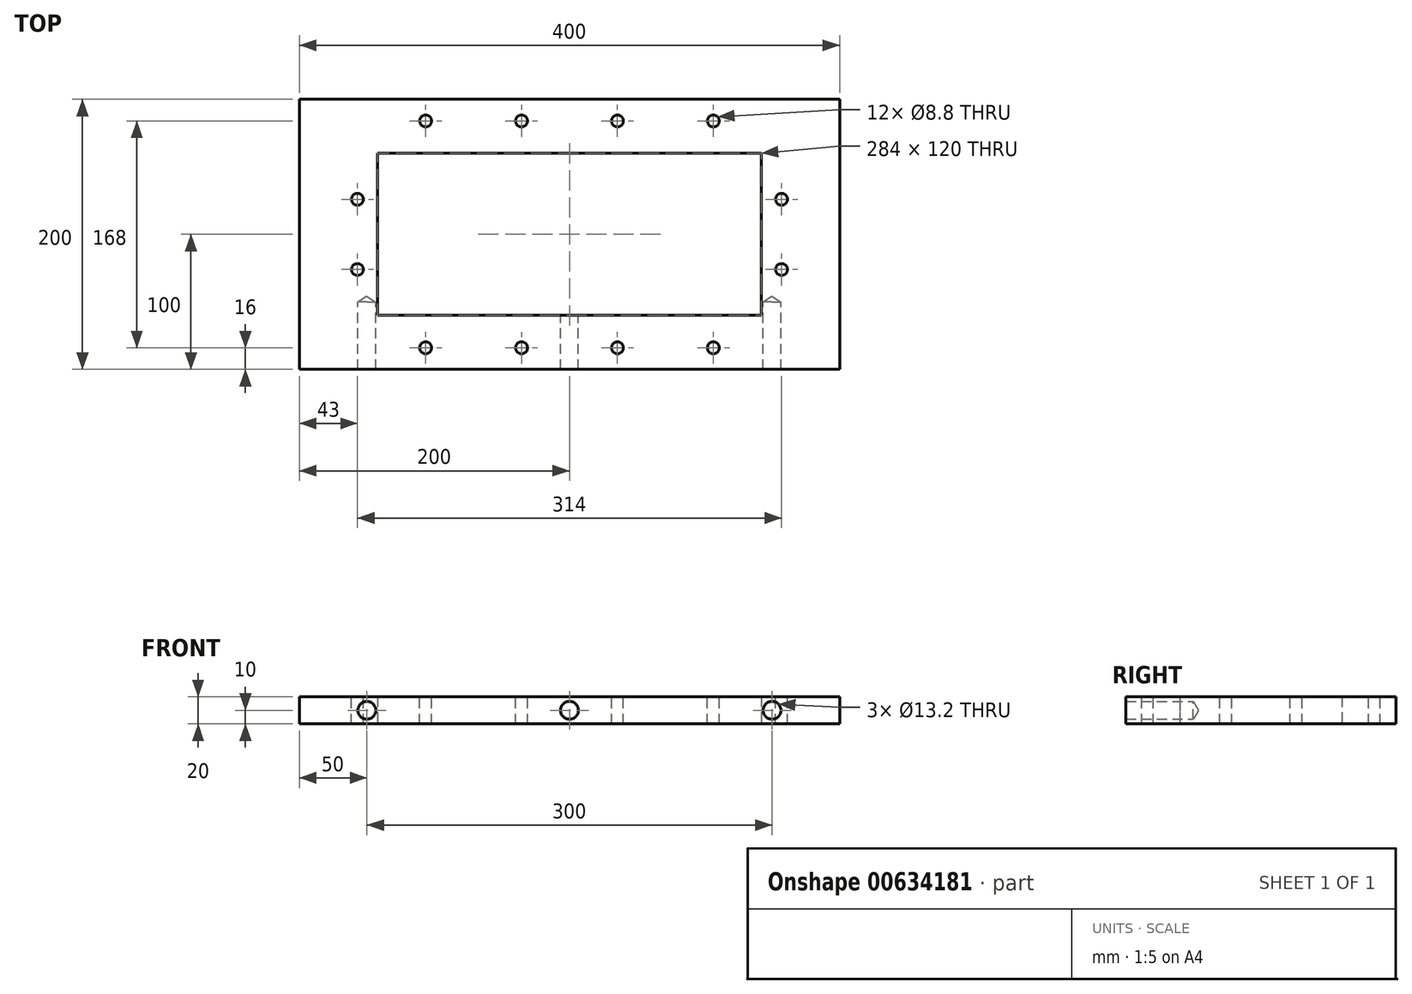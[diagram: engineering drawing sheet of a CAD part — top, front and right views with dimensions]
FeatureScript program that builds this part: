
annotation { "Feature Type Name" : "Feature", "Feature Type Description" : "" }
export const myFeature = defineFeature(function(context is Context, id is Id, definition is map)
    precondition{}
    {
        {
            var Q0;
            Q0=qCreatedBy(makeId("Top.planeOp"),FACE);
            var sketch = newSketch(context, id + "F0", { "sketchPlane" : qUnion([Q0])});
            skLineSegment(sketch, "E0.bottom", {"start": v(-200, 200) * mm, "end": v(200, 200) * mm});
            skLineSegment(sketch, "E0.top", {"start": v(-200, 0) * mm, "end": v(200, 0) * mm});
            skLineSegment(sketch, "E0.left", {"start": v(-200, 200) * mm, "end": v(-200, 0) * mm});
            skLineSegment(sketch, "E0.right", {"start": v(200, 200) * mm, "end": v(200, 0) * mm});
            skLineSegment(sketch, "E1.bottom", {"start": v(-142, 160) * mm, "end": v(142, 160) * mm});
            skLineSegment(sketch, "E1.top", {"start": v(-142, 40) * mm, "end": v(142, 40) * mm});
            skLineSegment(sketch, "E1.left", {"start": v(-142, 160) * mm, "end": v(-142, 40) * mm});
            skLineSegment(sketch, "E1.right", {"start": v(142, 160) * mm, "end": v(142, 40) * mm});
            skLineSegment(sketch, "E2.bottom", {"start": v(-157, 184) * mm, "end": v(157, 184) * mm, "construction": true});
            skLineSegment(sketch, "E2.top", {"start": v(-157, 16) * mm, "end": v(157, 16) * mm, "construction": true});
            skLineSegment(sketch, "E2.left", {"start": v(-157, 184) * mm, "end": v(-157, 16) * mm, "construction": true});
            skLineSegment(sketch, "E2.right", {"start": v(157, 184) * mm, "end": v(157, 16) * mm, "construction": true});
            skLineSegment(sketch, "E3", {"start": v(-106.5, 184) * mm, "end": v(-106.5, 16) * mm, "construction": true});
            skLineSegment(sketch, "E4", {"start": v(-35.5, 184) * mm, "end": v(-35.5, 16) * mm, "construction": true});
            skLineSegment(sketch, "E5", {"start": v(35.5, 184) * mm, "end": v(35.5, 16) * mm, "construction": true});
            skLineSegment(sketch, "E6", {"start": v(106.5, 184) * mm, "end": v(106.5, 16) * mm, "construction": true});
            skPoint(sketch, "E7", {"position": v(157, 126) * mm});
            skPoint(sketch, "E8", {"position": v(157, 74) * mm});
            skPoint(sketch, "E9", {"position": v(-157, 74) * mm});
            skPoint(sketch, "E10", {"position": v(-157, 126) * mm});
            skSolve(sketch);
        }
        {
            var Q0;
            Q0=makeQuery(id+"F0.imprint","IMPRINT",FACE,{"disambiguationData":[TD([[makeQuery(id+"F0.imprint","IMPRINT",EDGE,{"derivedFrom":sQuery(id+"F0.wireOp",EDGE,"E0.bottom")}),-1.0]])]});
            extrude(context, id + "F1", {"entities" : qUnion([Q0]), "depth" : 20 * mm, "offsetDistance" : 25 * mm});
        }
        {
            var Q0;
            Q0=sQuery(id+"F0.wireOp",VERTEX,"E10");
            var Q1;
            Q1=sQuery(id+"F0.wireOp",VERTEX,"E9");
            var Q2;
            Q2=sQuery(id+"F0.wireOp",VERTEX,"E3.end");
            var Q3;
            Q3=sQuery(id+"F0.wireOp",VERTEX,"E4.end");
            var Q4;
            Q4=sQuery(id+"F0.wireOp",VERTEX,"E5.end");
            var Q5;
            Q5=sQuery(id+"F0.wireOp",VERTEX,"E6.end");
            var Q6;
            Q6=sQuery(id+"F0.wireOp",VERTEX,"E8");
            var Q7;
            Q7=sQuery(id+"F0.wireOp",VERTEX,"E7");
            var Q8;
            Q8=sQuery(id+"F0.wireOp",VERTEX,"E6.start");
            var Q9;
            Q9=sQuery(id+"F0.wireOp",VERTEX,"E5.start");
            var Q10;
            Q10=sQuery(id+"F0.wireOp",VERTEX,"E4.start");
            var Q11;
            Q11=sQuery(id+"F0.wireOp",VERTEX,"E3.start");
            var Q12;
            Q12=makeQuery(id+"F1.opExtrude","SWEPT_BODY",BODY,{"disambiguationData":[OSD([sQuery(id+"F0.wireOp",EDGE,"E0.bottom"),sQuery(id+"F0.wireOp",EDGE,"E0.top"),sQuery(id+"F0.wireOp",EDGE,"E0.left"),sQuery(id+"F0.wireOp",EDGE,"E0.right"),sQuery(id+"F0.wireOp",EDGE,"E1.bottom"),sQuery(id+"F0.wireOp",EDGE,"E1.top"),sQuery(id+"F0.wireOp",EDGE,"E1.left"),sQuery(id+"F0.wireOp",EDGE,"E1.right")])]});
            hole(context, id + "F2", {"style" : HoleStyle.SIMPLE, "endStyle" : HoleEndStyle.THROUGH, "oppositeDirection" : true, "standardTappedOrClearance" : lookupTablePath({ "standard" : "ISO", "fit" : "Normal", "size" : "M8", "type" : "Clearance" }), "standardBlindInLast" : lookupTablePath({ "fit" : "Standard", "standard" : "ISO", "size" : "M8", "type" : "Clearance" }), "holeDiameter" : 8.8 * mm, "majorDiameter" : 5 * mm, "isTappedThrough" : true, "tappedDepth" : 20 * mm, "tapClearance" : 3, "locations" : qUnion([Q0, Q1, Q2, Q3, Q4, Q5, Q6, Q7, Q8, Q9, Q10, Q11]), "scope" : qUnion([Q12])});
        }
        {
            var Q0;
            Q0=qCreatedBy(makeId("Front.planeOp"),FACE);
            var sketch = newSketch(context, id + "F3", { "sketchPlane" : qUnion([Q0])});
            skLineSegment(sketch, "E11", {"start": v(-150, 10) * mm, "end": v(150, 10) * mm, "construction": true});
            skPoint(sketch, "E12", {"position": v(0, 10) * mm});
            skSolve(sketch);
        }
        {
            var Q0;
            Q0=sQuery(id+"F3.wireOp",VERTEX,"E11.start");
            var Q1;
            Q1=sQuery(id+"F3.wireOp",VERTEX,"E11.end");
            var Q2;
            Q2=sQuery(id+"F3.wireOp",VERTEX,"E12");
            var Q3;
            Q3=makeQuery(id+"F1.opExtrude","SWEPT_BODY",BODY,{"disambiguationData":[OSD([sQuery(id+"F0.wireOp",EDGE,"E0.bottom"),sQuery(id+"F0.wireOp",EDGE,"E0.top"),sQuery(id+"F0.wireOp",EDGE,"E0.left"),sQuery(id+"F0.wireOp",EDGE,"E0.right")])]});
            hole(context, id + "F4", {"style" : HoleStyle.SIMPLE, "endStyle" : HoleEndStyle.BLIND, "standardTappedOrClearance" : lookupTablePath({ "standard" : "ISO", "fit" : "Normal", "size" : "M12", "type" : "Clearance" }), "standardBlindInLast" : lookupTablePath({ "fit" : "Standard", "standard" : "ISO", "size" : "M12", "type" : "Clearance" }), "holeDiameter" : 13.2 * mm, "majorDiameter" : 5 * mm, "holeDepth" : 50 * mm, "isTappedThrough" : true, "tappedDepth" : 20 * mm, "tapClearance" : 3, "locations" : qUnion([Q0, Q1, Q2]), "scope" : qUnion([Q3])});
        }
    });
